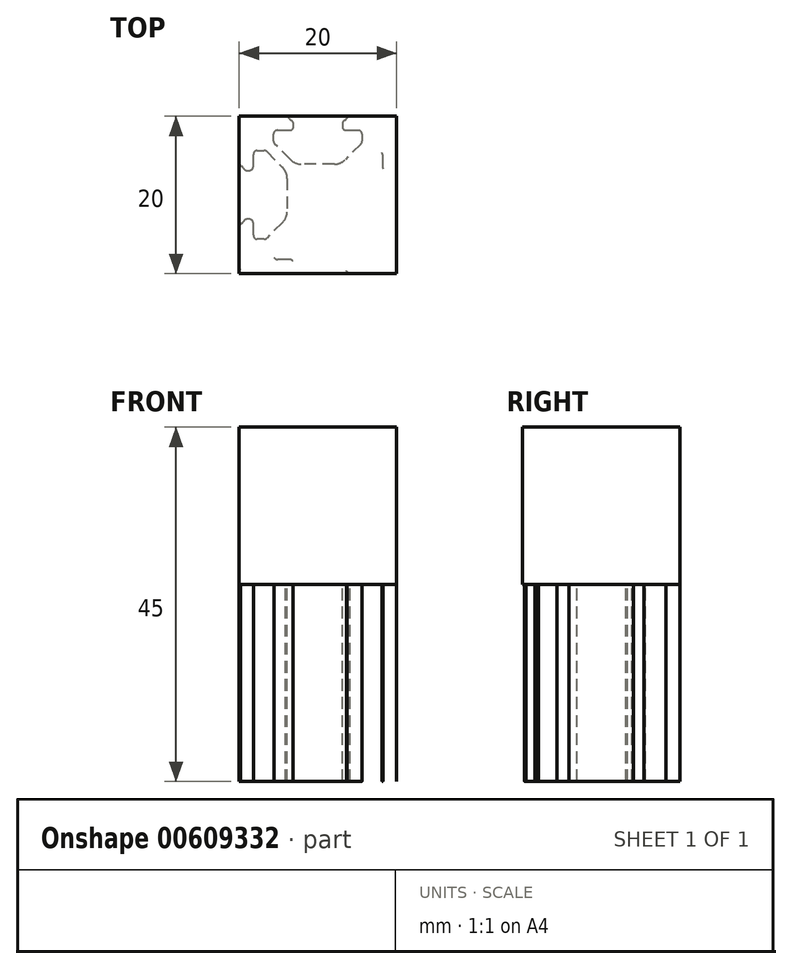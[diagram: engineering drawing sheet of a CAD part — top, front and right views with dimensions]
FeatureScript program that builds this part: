
annotation { "Feature Type Name" : "Feature", "Feature Type Description" : "" }
export const myFeature = defineFeature(function(context is Context, id is Id, definition is map)
    precondition{}
    {
        {
            var Q0;
            Q0=qCreatedBy(makeId("Top.planeOp"),FACE);
            var sketch = newSketch(context, id + "F0", { "sketchPlane" : qUnion([Q0])});
            skCircle(sketch, "E0", {"center": v(-10.39, -7.92) * mm, "radius": 2.5 * mm});
            skLineSegment(sketch, "E1", {"start": v(-13.49, 0.78) * mm, "end": v(-13.49, 1.08) * mm});
            skArc(sketch, "E2", {"start": v(-13.99, 0.28) * mm, "mid": v(-13.64, 0.43) * mm, "end": v(-13.49, 0.78) * mm});
            skLineSegment(sketch, "E3", {"start": v(-15.52, 0.28) * mm, "end": v(-13.99, 0.28) * mm});
            skArc(sketch, "E4", {"start": v(-16.02, -0.22) * mm, "mid": v(-15.87, 0.14) * mm, "end": v(-15.52, 0.28) * mm});
            skLineSegment(sketch, "E5", {"start": v(-16.02, -1.1) * mm, "end": v(-16.02, -0.22) * mm});
            skArc(sketch, "E6", {"start": v(-15.87, -1.44) * mm, "mid": v(-15.98, -1.28) * mm, "end": v(-16.02, -1.1) * mm});
            skLineSegment(sketch, "E7", {"start": v(-13.89, -3.43) * mm, "end": v(-15.87, -1.44) * mm});
            skArc(sketch, "E8", {"start": v(-12.47, -4.02) * mm, "mid": v(-13.24, -3.87) * mm, "end": v(-13.89, -3.43) * mm});
            skLineSegment(sketch, "E9", {"start": v(-8.3, -4.02) * mm, "end": v(-12.47, -4.02) * mm});
            skArc(sketch, "E10", {"start": v(-6.9, -3.43) * mm, "mid": v(-7.54, -3.87) * mm, "end": v(-8.3, -4.02) * mm});
            skLineSegment(sketch, "E11", {"start": v(-4.9, -1.44) * mm, "end": v(-6.9, -3.43) * mm});
            skArc(sketch, "E12", {"start": v(-4.76, -1.1) * mm, "mid": v(-4.8, -1.28) * mm, "end": v(-4.9, -1.44) * mm});
            skLineSegment(sketch, "E13", {"start": v(-4.76, -0.22) * mm, "end": v(-4.76, -1.1) * mm});
            skArc(sketch, "E14", {"start": v(-5.26, 0.28) * mm, "mid": v(-4.9, 0.14) * mm, "end": v(-4.76, -0.22) * mm});
            skLineSegment(sketch, "E15", {"start": v(-6.79, 0.28) * mm, "end": v(-5.26, 0.28) * mm});
            skArc(sketch, "E16", {"start": v(-7.29, 0.78) * mm, "mid": v(-7.14, 0.43) * mm, "end": v(-6.79, 0.28) * mm});
            skLineSegment(sketch, "E17", {"start": v(-7.29, 1.08) * mm, "end": v(-7.29, 0.78) * mm});
            skArc(sketch, "E18", {"start": v(-7, 1.54) * mm, "mid": v(-7.2, 1.35) * mm, "end": v(-7.29, 1.08) * mm});
            skArc(sketch, "E19", {"start": v(-6.74, 1.79) * mm, "mid": v(-6.85, 1.64) * mm, "end": v(-7, 1.54) * mm});
            skArc(sketch, "E20", {"start": v(-6.29, 2.08) * mm, "mid": v(-6.56, 2) * mm, "end": v(-6.75, 1.79) * mm});
            skLineSegment(sketch, "E21", {"start": v(-1.39, 2.08) * mm, "end": v(-6.29, 2.08) * mm});
            skArc(sketch, "E22", {"start": v(-0.39, 1.08) * mm, "mid": v(-0.68, 1.79) * mm, "end": v(-1.39, 2.08) * mm});
            skArc(sketch, "E23", {"start": v(-0.68, -4.27) * mm, "mid": v(-0.47, -4.09) * mm, "end": v(-0.39, -3.82) * mm});
            skArc(sketch, "E24", {"start": v(-0.93, -4.52) * mm, "mid": v(-0.83, -4.38) * mm, "end": v(-0.68, -4.27) * mm});
            skArc(sketch, "E25", {"start": v(-1.39, -4.82) * mm, "mid": v(-1.12, -4.74) * mm, "end": v(-0.93, -4.52) * mm});
            skLineSegment(sketch, "E26", {"start": v(-1.69, -4.82) * mm, "end": v(-1.39, -4.82) * mm});
            skArc(sketch, "E27", {"start": v(-2.19, -4.32) * mm, "mid": v(-2.04, -4.67) * mm, "end": v(-1.69, -4.82) * mm});
            skLineSegment(sketch, "E28", {"start": v(-2.19, -2.79) * mm, "end": v(-2.19, -4.32) * mm});
            skArc(sketch, "E29", {"start": v(-2.69, -2.29) * mm, "mid": v(-2.34, -2.43) * mm, "end": v(-2.19, -2.79) * mm});
            skLineSegment(sketch, "E30", {"start": v(-3.56, -2.29) * mm, "end": v(-2.69, -2.29) * mm});
            skArc(sketch, "E31", {"start": v(-3.92, -2.43) * mm, "mid": v(-3.75, -2.33) * mm, "end": v(-3.56, -2.29) * mm});
            skLineSegment(sketch, "E32", {"start": v(-5.9, -4.42) * mm, "end": v(-3.92, -2.43) * mm});
            skArc(sketch, "E33", {"start": v(-6.49, -5.84) * mm, "mid": v(-6.34, -5.07) * mm, "end": v(-5.9, -4.42) * mm});
            skLineSegment(sketch, "E34", {"start": v(-6.49, -10) * mm, "end": v(-6.49, -5.84) * mm});
            skArc(sketch, "E35", {"start": v(-5.9, -11.41) * mm, "mid": v(-6.34, -10.76) * mm, "end": v(-6.49, -10) * mm});
            skLineSegment(sketch, "E36", {"start": v(-3.92, -13.4) * mm, "end": v(-5.9, -11.41) * mm});
            skArc(sketch, "E37", {"start": v(-3.56, -13.55) * mm, "mid": v(-3.75, -13.5) * mm, "end": v(-3.92, -13.4) * mm});
            skLineSegment(sketch, "E38", {"start": v(-2.69, -13.55) * mm, "end": v(-3.56, -13.55) * mm});
            skArc(sketch, "E39", {"start": v(-2.19, -13.05) * mm, "mid": v(-2.34, -13.4) * mm, "end": v(-2.69, -13.55) * mm});
            skLineSegment(sketch, "E40", {"start": v(-2.19, -11.52) * mm, "end": v(-2.19, -13.05) * mm});
            skArc(sketch, "E41", {"start": v(-1.69, -11.02) * mm, "mid": v(-2.04, -11.16) * mm, "end": v(-2.19, -11.52) * mm});
            skLineSegment(sketch, "E42", {"start": v(-1.39, -11.02) * mm, "end": v(-1.69, -11.02) * mm});
            skArc(sketch, "E43", {"start": v(-0.93, -11.31) * mm, "mid": v(-1.12, -11.1) * mm, "end": v(-1.39, -11.02) * mm});
            skArc(sketch, "E44", {"start": v(-0.68, -11.56) * mm, "mid": v(-0.83, -11.46) * mm, "end": v(-0.93, -11.31) * mm});
            skArc(sketch, "E45", {"start": v(-0.39, -12.02) * mm, "mid": v(-0.47, -11.75) * mm, "end": v(-0.68, -11.56) * mm});
            skLineSegment(sketch, "E46", {"start": v(-0.39, -16.92) * mm, "end": v(-0.39, -12.02) * mm});
            skArc(sketch, "E47", {"start": v(-1.39, -17.92) * mm, "mid": v(-0.68, -17.62) * mm, "end": v(-0.39, -16.92) * mm});
            skLineSegment(sketch, "E48", {"start": v(-6.29, -17.92) * mm, "end": v(-1.39, -17.92) * mm});
            skArc(sketch, "E49", {"start": v(-6.75, -17.62) * mm, "mid": v(-6.56, -17.84) * mm, "end": v(-6.29, -17.92) * mm});
            skArc(sketch, "E50", {"start": v(-7, -17.37) * mm, "mid": v(-6.85, -17.48) * mm, "end": v(-6.74, -17.62) * mm});
            skArc(sketch, "E51", {"start": v(-7.29, -16.92) * mm, "mid": v(-7.2, -17.19) * mm, "end": v(-7, -17.37) * mm});
            skLineSegment(sketch, "E52", {"start": v(-7.29, -16.62) * mm, "end": v(-7.29, -16.92) * mm});
            skArc(sketch, "E53", {"start": v(-6.79, -16.12) * mm, "mid": v(-7.14, -16.26) * mm, "end": v(-7.29, -16.62) * mm});
            skLineSegment(sketch, "E54", {"start": v(-5.26, -16.12) * mm, "end": v(-6.79, -16.12) * mm});
            skArc(sketch, "E55", {"start": v(-4.76, -15.62) * mm, "mid": v(-4.9, -15.97) * mm, "end": v(-5.26, -16.12) * mm});
            skLineSegment(sketch, "E56", {"start": v(-4.76, -14.74) * mm, "end": v(-4.76, -15.62) * mm});
            skArc(sketch, "E57", {"start": v(-4.9, -14.4) * mm, "mid": v(-4.8, -14.55) * mm, "end": v(-4.76, -14.74) * mm});
            skLineSegment(sketch, "E58", {"start": v(-6.9, -12.4) * mm, "end": v(-4.9, -14.4) * mm});
            skArc(sketch, "E59", {"start": v(-8.3, -11.82) * mm, "mid": v(-7.54, -11.97) * mm, "end": v(-6.9, -12.4) * mm});
            skLineSegment(sketch, "E60", {"start": v(-12.47, -11.82) * mm, "end": v(-8.3, -11.82) * mm});
            skArc(sketch, "E61", {"start": v(-13.89, -12.4) * mm, "mid": v(-13.24, -11.97) * mm, "end": v(-12.47, -11.82) * mm});
            skLineSegment(sketch, "E62", {"start": v(-15.87, -14.4) * mm, "end": v(-13.89, -12.4) * mm});
            skArc(sketch, "E63", {"start": v(-16.02, -14.74) * mm, "mid": v(-15.98, -14.55) * mm, "end": v(-15.87, -14.4) * mm});
            skLineSegment(sketch, "E64", {"start": v(-16.02, -15.62) * mm, "end": v(-16.02, -14.74) * mm});
            skArc(sketch, "E65", {"start": v(-15.52, -16.12) * mm, "mid": v(-15.87, -15.97) * mm, "end": v(-16.02, -15.62) * mm});
            skLineSegment(sketch, "E66", {"start": v(-13.99, -16.12) * mm, "end": v(-15.52, -16.12) * mm});
            skArc(sketch, "E67", {"start": v(-13.49, -16.62) * mm, "mid": v(-13.64, -16.26) * mm, "end": v(-13.99, -16.12) * mm});
            skLineSegment(sketch, "E68", {"start": v(-13.49, -16.92) * mm, "end": v(-13.49, -16.62) * mm});
            skArc(sketch, "E69", {"start": v(-13.78, -17.37) * mm, "mid": v(-13.57, -17.19) * mm, "end": v(-13.49, -16.92) * mm});
            skArc(sketch, "E70", {"start": v(-14.03, -17.62) * mm, "mid": v(-13.93, -17.48) * mm, "end": v(-13.78, -17.37) * mm});
            skArc(sketch, "E71", {"start": v(-14.49, -17.92) * mm, "mid": v(-14.22, -17.84) * mm, "end": v(-14.03, -17.62) * mm});
            skArc(sketch, "E72", {"start": v(-20.39, -16.92) * mm, "mid": v(-20.1, -17.62) * mm, "end": v(-19.39, -17.92) * mm});
            skArc(sketch, "E73", {"start": v(-20.1, -11.56) * mm, "mid": v(-20.3, -11.75) * mm, "end": v(-20.39, -12.02) * mm});
            skArc(sketch, "E74", {"start": v(-19.85, -11.31) * mm, "mid": v(-19.95, -11.46) * mm, "end": v(-20.1, -11.56) * mm});
            skArc(sketch, "E75", {"start": v(-19.39, -11.02) * mm, "mid": v(-19.66, -11.1) * mm, "end": v(-19.85, -11.31) * mm});
            skLineSegment(sketch, "E76", {"start": v(-19.09, -11.02) * mm, "end": v(-19.39, -11.02) * mm});
            skArc(sketch, "E77", {"start": v(-18.59, -11.52) * mm, "mid": v(-18.74, -11.16) * mm, "end": v(-19.09, -11.02) * mm});
            skLineSegment(sketch, "E78", {"start": v(-18.59, -13.05) * mm, "end": v(-18.59, -11.52) * mm});
            skArc(sketch, "E79", {"start": v(-18.09, -13.55) * mm, "mid": v(-18.44, -13.4) * mm, "end": v(-18.59, -13.05) * mm});
            skLineSegment(sketch, "E80", {"start": v(-17.22, -13.55) * mm, "end": v(-18.09, -13.55) * mm});
            skArc(sketch, "E81", {"start": v(-16.86, -13.4) * mm, "mid": v(-17.03, -13.5) * mm, "end": v(-17.22, -13.55) * mm});
            skLineSegment(sketch, "E82", {"start": v(-14.88, -11.41) * mm, "end": v(-16.86, -13.4) * mm});
            skArc(sketch, "E83", {"start": v(-14.29, -10) * mm, "mid": v(-14.44, -10.76) * mm, "end": v(-14.88, -11.41) * mm});
            skLineSegment(sketch, "E84", {"start": v(-14.29, -5.84) * mm, "end": v(-14.29, -10) * mm});
            skArc(sketch, "E85", {"start": v(-14.88, -4.42) * mm, "mid": v(-14.44, -5.07) * mm, "end": v(-14.29, -5.84) * mm});
            skLineSegment(sketch, "E86", {"start": v(-16.86, -2.43) * mm, "end": v(-14.88, -4.42) * mm});
            skArc(sketch, "E87", {"start": v(-17.22, -2.29) * mm, "mid": v(-17.03, -2.33) * mm, "end": v(-16.86, -2.43) * mm});
            skLineSegment(sketch, "E88", {"start": v(-18.09, -2.29) * mm, "end": v(-17.22, -2.29) * mm});
            skArc(sketch, "E89", {"start": v(-18.59, -2.79) * mm, "mid": v(-18.44, -2.43) * mm, "end": v(-18.09, -2.29) * mm});
            skLineSegment(sketch, "E90", {"start": v(-18.59, -4.32) * mm, "end": v(-18.59, -2.79) * mm});
            skArc(sketch, "E91", {"start": v(-19.09, -4.82) * mm, "mid": v(-18.74, -4.67) * mm, "end": v(-18.59, -4.32) * mm});
            skLineSegment(sketch, "E92", {"start": v(-19.39, -4.82) * mm, "end": v(-19.09, -4.82) * mm});
            skArc(sketch, "E93", {"start": v(-19.85, -4.52) * mm, "mid": v(-19.66, -4.74) * mm, "end": v(-19.39, -4.82) * mm});
            skArc(sketch, "E94", {"start": v(-20.1, -4.27) * mm, "mid": v(-19.95, -4.38) * mm, "end": v(-19.85, -4.52) * mm});
            skArc(sketch, "E95", {"start": v(-20.39, -3.82) * mm, "mid": v(-20.3, -4.09) * mm, "end": v(-20.1, -4.27) * mm});
            skLineSegment(sketch, "E96", {"start": v(-20.39, 1.08) * mm, "end": v(-20.39, -3.82) * mm});
            skArc(sketch, "E97", {"start": v(-19.39, 2.08) * mm, "mid": v(-20.1, 1.79) * mm, "end": v(-20.39, 1.08) * mm});
            skLineSegment(sketch, "E98", {"start": v(-14.49, 2.08) * mm, "end": v(-19.39, 2.08) * mm});
            skArc(sketch, "E99", {"start": v(-14.03, 1.79) * mm, "mid": v(-14.22, 2) * mm, "end": v(-14.49, 2.08) * mm});
            skArc(sketch, "E100", {"start": v(-13.78, 1.54) * mm, "mid": v(-13.93, 1.64) * mm, "end": v(-14.03, 1.79) * mm});
            skArc(sketch, "E101", {"start": v(-13.49, 1.08) * mm, "mid": v(-13.57, 1.35) * mm, "end": v(-13.78, 1.54) * mm});
            skArc(sketch, "E102", {"start": v(-12.47, -4.02) * mm, "mid": v(-13.24, -3.86) * mm, "end": v(-13.89, -3.43) * mm});
            skArc(sketch, "E103", {"start": v(-6.9, -3.43) * mm, "mid": v(-7.54, -3.86) * mm, "end": v(-8.3, -4.02) * mm});
            skArc(sketch, "E104", {"start": v(-6.75, 1.79) * mm, "mid": v(-6.85, 1.64) * mm, "end": v(-7, 1.54) * mm});
            skLineSegment(sketch, "E105", {"start": v(-0.39, -3.82) * mm, "end": v(-0.39, 1.08) * mm});
            skArc(sketch, "E106", {"start": v(-7, -17.37) * mm, "mid": v(-6.85, -17.48) * mm, "end": v(-6.75, -17.62) * mm});
            skLineSegment(sketch, "E107", {"start": v(-19.39, -17.92) * mm, "end": v(-14.49, -17.92) * mm});
            skLineSegment(sketch, "E108", {"start": v(-20.39, -12.02) * mm, "end": v(-20.39, -16.92) * mm});
            skLineSegment(sketch, "E109", {"start": v(-14.49, 2.08) * mm, "end": v(-6.29, 2.08) * mm});
            skLineSegment(sketch, "E110", {"start": v(-0.39, -3.82) * mm, "end": v(-0.39, -12.02) * mm});
            skLineSegment(sketch, "E111", {"start": v(-20.39, -3.82) * mm, "end": v(-20.39, -12.02) * mm});
            skLineSegment(sketch, "E112", {"start": v(-14.49, -17.92) * mm, "end": v(-6.29, -17.92) * mm});
            skLineSegment(sketch, "E113", {"start": v(-20.39, 1.08) * mm, "end": v(-20.39, -16.92) * mm});
            skLineSegment(sketch, "E114", {"start": v(-19.39, -17.92) * mm, "end": v(-1.39, -17.92) * mm});
            skLineSegment(sketch, "E115", {"start": v(-0.39, -16.92) * mm, "end": v(-0.39, 1.08) * mm});
            skLineSegment(sketch, "E116", {"start": v(-1.39, 2.08) * mm, "end": v(-19.39, 2.08) * mm});
            skSolve(sketch);
        }
        {
            var Q0;
            {var subQ4=sQuery(id+"F0.wireOp",EDGE,"E17");Q0=makeQuery(id+"F0.imprint","IMPRINT",FACE,{"disambiguationData":[TD([[makeQuery(id+"F0.imprint","IMPRINT",EDGE,{"derivedFrom":subQ4}),-1.0]])]});}
            var Q1;
            {var subQ5=sQuery(id+"F0.wireOp",EDGE,"E28");Q1=makeQuery(id+"F0.imprint","IMPRINT",FACE,{"disambiguationData":[TD([[makeQuery(id+"F0.imprint","IMPRINT",EDGE,{"derivedFrom":subQ5}),-1.0]])]});}
            var Q2;
            {var subQ5=sQuery(id+"F0.wireOp",EDGE,"E66");Q2=makeQuery(id+"F0.imprint","IMPRINT",FACE,{"disambiguationData":[TD([[makeQuery(id+"F0.imprint","IMPRINT",EDGE,{"derivedFrom":subQ5}),-1.0]])]});}
            var Q3;
            {var subQ5=sQuery(id+"F0.wireOp",EDGE,"E73");Q3=makeQuery(id+"F0.imprint","IMPRINT",FACE,{"disambiguationData":[TD([[makeQuery(id+"F0.imprint","IMPRINT",EDGE,{"derivedFrom":subQ5}),-1.0]])]});}
            var Q4;
            {var subQ0=sQuery(id+"F0.wireOp",EDGE,"E111");var subQ1=sQuery(id+"F0.wireOp",EDGE,"E95");var subQ2=makeQuery(id+"F0.imprint","INTERSECT",VERTEX,{"derivedFrom":[subQ1,subQ0]});Q4=makeQuery(id+"F0.imprint","IMPRINT",FACE,{"disambiguationData":[TD([[makeQuery(id+"F0.imprint","IMPRINT",EDGE,{"disambiguationData":[TD([[subQ2,-1.0]])],"derivedFrom":subQ1}),-1.0]])]});}
            var Q5;
            {var subQ0=sQuery(id+"F0.wireOp",EDGE,"E99");Q5=makeQuery(id+"F0.imprint","IMPRINT",FACE,{"disambiguationData":[TD([[makeQuery(id+"F0.imprint","IMPRINT",EDGE,{"derivedFrom":subQ0}),-1.0]])]});}
            var Q6;
            Q6=makeQuery(id+"F0.imprint","IMPRINT",FACE,{"disambiguationData":[TD([[makeQuery(id+"F0.imprint","IMPRINT",EDGE,{"derivedFrom":sQuery(id+"F0.wireOp",EDGE,"E23")}),-1.0]])]});
            var Q7;
            {var subQ6=sQuery(id+"F0.wireOp",EDGE,"E49");Q7=makeQuery(id+"F0.imprint","IMPRINT",FACE,{"disambiguationData":[TD([[makeQuery(id+"F0.imprint","IMPRINT",EDGE,{"derivedFrom":subQ6}),-1.0]])]});}
            var Q8;
            {var subQ16=sQuery(id+"F0.wireOp",EDGE,"E78");Q8=makeQuery(id+"F0.imprint","IMPRINT",FACE,{"disambiguationData":[TD([[makeQuery(id+"F0.imprint","IMPRINT",EDGE,{"derivedFrom":subQ16}),-1.0]])]});}
            var Q9;
            {var subQ13=sQuery(id+"F0.wireOp",EDGE,"E1");Q9=makeQuery(id+"F0.imprint","IMPRINT",FACE,{"disambiguationData":[TD([[makeQuery(id+"F0.imprint","IMPRINT",EDGE,{"derivedFrom":subQ13}),-1.0]])]});}
            extrude(context, id + "F1", {"entities" : qUnion([Q0, Q1, Q2, Q3, Q4, Q5, Q6, Q7, Q8, Q9]), "depth" : -25 * mm, "offsetDistance" : 25 * mm});
        }
        {
            var Q0;
            Q0=makeQuery(id+"F1.opExtrude","CAP_FACE",FACE,{"disambiguationData":[OSD([sQuery(id+"F0.wireOp",EDGE,"E1"),sQuery(id+"F0.wireOp",EDGE,"E2"),sQuery(id+"F0.wireOp",EDGE,"E3"),sQuery(id+"F0.wireOp",EDGE,"E4"),sQuery(id+"F0.wireOp",EDGE,"E5"),sQuery(id+"F0.wireOp",EDGE,"E6"),sQuery(id+"F0.wireOp",EDGE,"E14"),sQuery(id+"F0.wireOp",EDGE,"E15"),sQuery(id+"F0.wireOp",EDGE,"E16"),sQuery(id+"F0.wireOp",EDGE,"E17"),sQuery(id+"F0.wireOp",EDGE,"E18"),sQuery(id+"F0.wireOp",EDGE,"E19"),sQuery(id+"F0.wireOp",EDGE,"E20"),sQuery(id+"F0.wireOp",EDGE,"E99"),sQuery(id+"F0.wireOp",EDGE,"E101"),sQuery(id+"F0.wireOp",EDGE,"E6"),sQuery(id+"F0.wireOp",EDGE,"E7"),sQuery(id+"F0.wireOp",EDGE,"E102"),sQuery(id+"F0.wireOp",EDGE,"E9"),sQuery(id+"F0.wireOp",EDGE,"E103"),sQuery(id+"F0.wireOp",EDGE,"E11"),sQuery(id+"F0.wireOp",EDGE,"E12"),sQuery(id+"F0.wireOp",EDGE,"E13"),sQuery(id+"F0.wireOp",EDGE,"E14"),sQuery(id+"F0.wireOp",EDGE,"E99"),sQuery(id+"F0.wireOp",EDGE,"E100"),sQuery(id+"F0.wireOp",EDGE,"E101"),sQuery(id+"F0.wireOp",EDGE,"E116")])],"isStart":true});
            var sketch = newSketch(context, id + "F2", { "sketchPlane" : qUnion([Q0])});
            skLineSegment(sketch, "E117.bottom", {"start": v(-0.39, -17.92) * mm, "end": v(-20.39, -17.92) * mm});
            skLineSegment(sketch, "E117.top", {"start": v(-0.39, 2.08) * mm, "end": v(-20.39, 2.08) * mm});
            skLineSegment(sketch, "E117.left", {"start": v(-0.39, -17.92) * mm, "end": v(-0.39, 2.08) * mm});
            skLineSegment(sketch, "E117.right", {"start": v(-20.39, -17.92) * mm, "end": v(-20.39, 2.08) * mm});
            skPoint(sketch, "E117.middle", {"position": v(-10.39, -7.92) * mm});
            skPoint(sketch, "E118.visualSharp", {"position": v(-20.39, 2.08) * mm});
            skPoint(sketch, "E119.visualSharp", {"position": v(-20.39, -17.92) * mm});
            skPoint(sketch, "E120.visualSharp", {"position": v(-0.39, -17.92) * mm});
            skPoint(sketch, "E121.visualSharp", {"position": v(-0.39, 2.08) * mm});
            skSolve(sketch);
        }
        {
            var Q0;
            Q0 = qSketchRegion(id + "F2", true);
            extrude(context, id + "F3", {"entities" : qUnion([Q0]), "depth" : 20 * mm, "offsetDistance" : 25 * mm});
        }
    });
